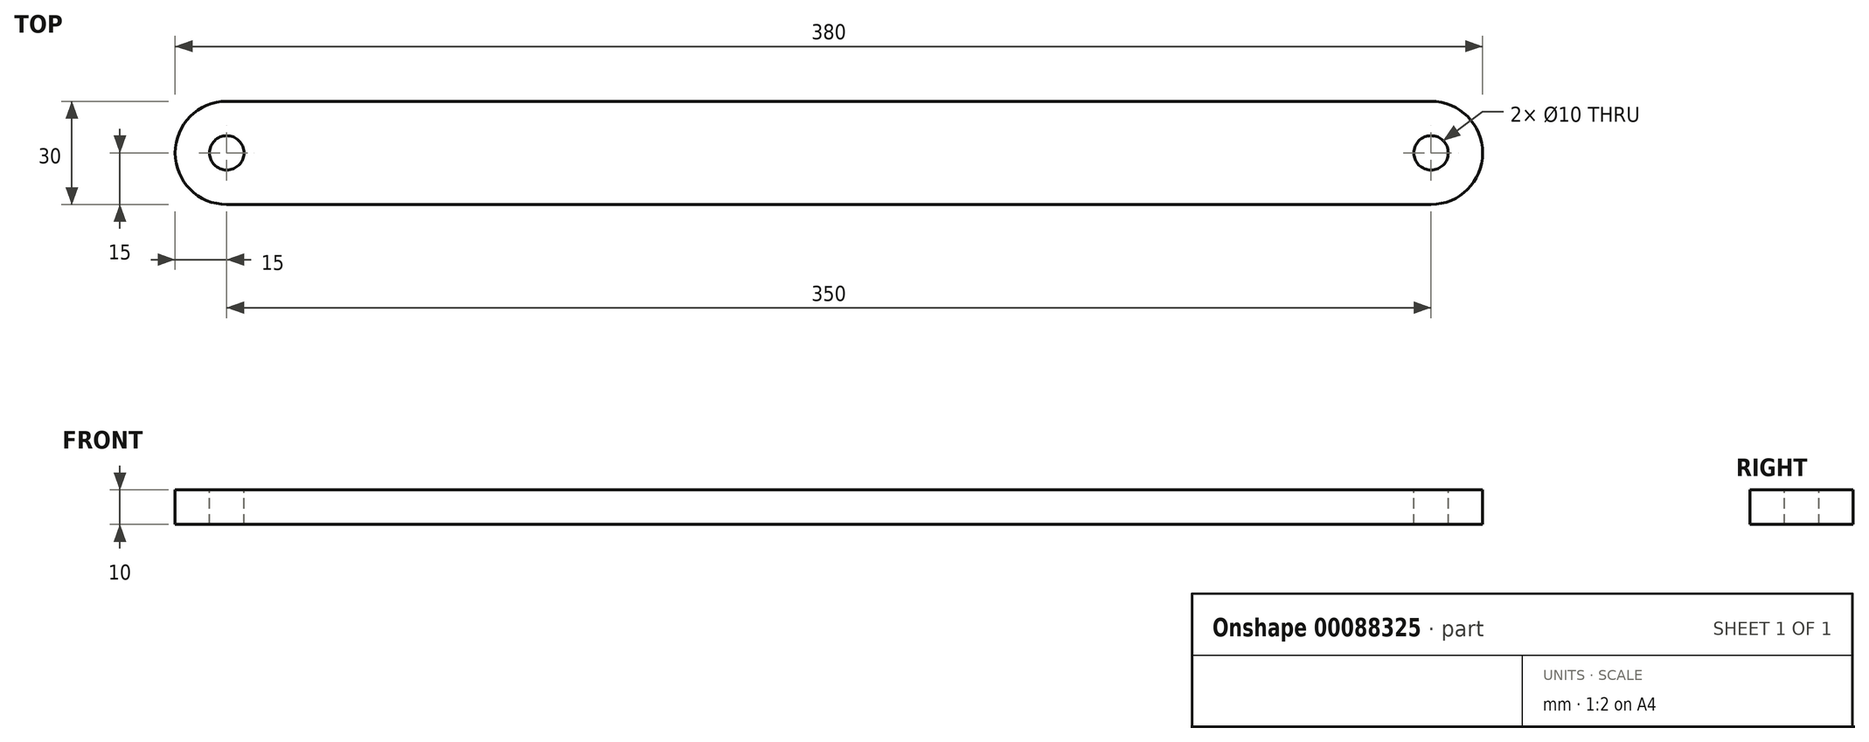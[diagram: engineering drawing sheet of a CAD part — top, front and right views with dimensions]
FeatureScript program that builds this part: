
annotation { "Feature Type Name" : "Feature", "Feature Type Description" : "" }
export const myFeature = defineFeature(function(context is Context, id is Id, definition is map)
    precondition{}
    {
        {
            var Q0;
            Q0=qCreatedBy(makeId("Top.planeOp"),FACE);
            var sketch = newSketch(context, id + "F0", { "sketchPlane" : qUnion([Q0])});
            skLineSegment(sketch, "E0", {"start": v(0, 15) * mm, "end": v(350, 15) * mm});
            skArc(sketch, "E1", {"start": v(350, 15) * mm, "mid": v(365, 0) * mm, "end": v(350, -15) * mm});
            skArc(sketch, "E2", {"start": v(0, 15) * mm, "mid": v(-15, 0) * mm, "end": v(0, -15) * mm});
            skLineSegment(sketch, "E3", {"start": v(0, -15) * mm, "end": v(350, -15) * mm});
            skSolve(sketch);
        }
        {
            var Q0;
            Q0=qSketchRegion(id+"F0",true);
            extrude(context, id + "F1", {"entities" : qUnion([Q0]), "depth" : 10 * mm});
        }
        {
            var Q0;
            Q0=makeQuery(id+"F1.opExtrude","CAP_FACE",FACE,{"disambiguationData":[OSD([sQuery(id+"F0.wireOp",EDGE,"E0"),sQuery(id+"F0.wireOp",EDGE,"E1"),sQuery(id+"F0.wireOp",EDGE,"E2"),sQuery(id+"F0.wireOp",EDGE,"E3")])],"isStart":false});
            var sketch = newSketch(context, id + "F2", { "sketchPlane" : qUnion([Q0])});
            skCircle(sketch, "E4", {"center": v(0, 0) * mm, "radius": 5 * mm});
            skCircle(sketch, "E5", {"center": v(350, 0) * mm, "radius": 5 * mm});
            skSolve(sketch);
        }
        {
            var Q0;
            Q0=qSketchRegion(id+"F2",true);
            extrude(context, id + "F3", {"entities" : qUnion([Q0]), "operationType" : NewBodyOperationType.REMOVE, "endBound" : BoundingType.THROUGH_ALL, "oppositeDirection" : true, "depth" : 25 * mm});
        }
    });
